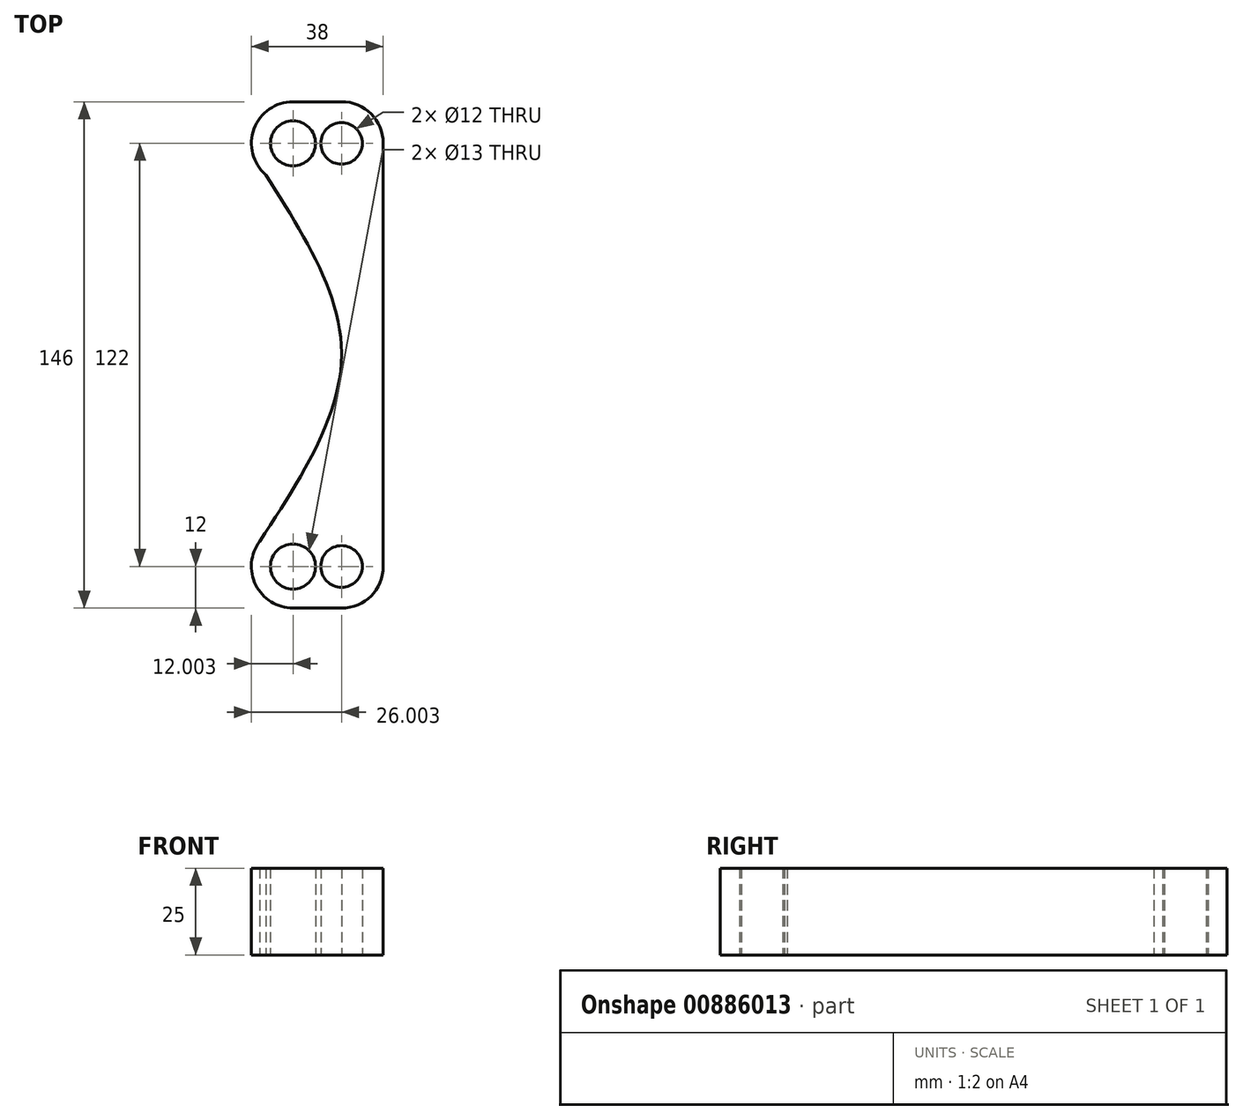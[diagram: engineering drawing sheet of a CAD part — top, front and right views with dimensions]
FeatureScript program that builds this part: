
annotation { "Feature Type Name" : "Feature", "Feature Type Description" : "" }
export const myFeature = defineFeature(function(context is Context, id is Id, definition is map)
    precondition{}
    {
        {
            var Q0;
            Q0=qCreatedBy(makeId("Top.planeOp"),FACE);
            var sketch = newSketch(context, id + "F0", { "sketchPlane" : qUnion([Q0])});
            skCircle(sketch, "E0", {"center": v(0, 0) * mm, "radius": 151 * mm, "construction": true});
            skCircle(sketch, "E1", {"center": v(0, 0) * mm, "radius": 70 * mm, "construction": true});
            skCircle(sketch, "E2", {"center": v(-34.34, 61) * mm, "radius": 6 * mm});
            skCircle(sketch, "E3", {"center": v(-34.34, -61) * mm, "radius": 6 * mm});
            skLineSegment(sketch, "E4", {"start": v(-34.34, -61) * mm, "end": v(-34.34, 61) * mm});
            skLineSegment(sketch, "E5", {"start": v(-151, 0) * mm, "end": v(-104, 0) * mm});
            skLineSegment(sketch, "E6", {"start": v(-70, 0) * mm, "end": v(-104, 0) * mm});
            skCircle(sketch, "E7", {"center": v(-48.34, 61) * mm, "radius": 6.5 * mm});
            skCircle(sketch, "E8", {"center": v(-48.34, -61) * mm, "radius": 6.5 * mm});
            skLineSegment(sketch, "E9", {"start": v(-34.34, -61) * mm, "end": v(-48.34, -61) * mm});
            skLineSegment(sketch, "E10", {"start": v(-34.34, 61) * mm, "end": v(-48.34, 61) * mm});
            skCircle(sketch, "E11", {"center": v(-34.34, 61) * mm, "radius": 12 * mm});
            skCircle(sketch, "E12", {"center": v(-48.34, 61) * mm, "radius": 12 * mm});
            skCircle(sketch, "E13", {"center": v(-48.34, -61) * mm, "radius": 12 * mm});
            skCircle(sketch, "E14", {"center": v(-34.34, -61) * mm, "radius": 12 * mm});
            skLineSegment(sketch, "E15", {"start": v(-22.34, -61) * mm, "end": v(-22.34, 61) * mm});
            skFitSpline(sketch, "E16", {"points": [v(-56.2, 51.93) * mm, v(-34.34, 0) * mm, v(-57.89, -53.74) * mm], "startDerivative": vector(66.64, -104.54) * mm, "endDerivative": vector(-69.54, -106.78) * mm});
            skLineSegment(sketch, "E17", {"start": v(-48.34, 73) * mm, "end": v(-34.34, 73) * mm});
            skLineSegment(sketch, "E18", {"start": v(-48.34, -73) * mm, "end": v(-34.34, -73) * mm});
            skSolve(sketch);
        }
        {
            var Q0;
            Q0 = qSketchRegion(id + "F0", true);
            var Q1;
            {var subQ5=sQuery(id+"F0.wireOp",EDGE,"E10");var subQ6=sQuery(id+"F0.wireOp",EDGE,"E2");var subQ7=makeQuery(id+"F0.imprint","INTERSECT",VERTEX,{"derivedFrom":[subQ6,subQ5]});Q1=makeQuery(id+"F0.imprint","IMPRINT",FACE,{"disambiguationData":[TD([[makeQuery(id+"F0.imprint","IMPRINT",EDGE,{"disambiguationData":[TD([[subQ7,-1.0]])],"derivedFrom":subQ6}),-1.0]])]});}
            var Q2;
            {var subQ5=sQuery(id+"F0.wireOp",EDGE,"E10");var subQ6=sQuery(id+"F0.wireOp",EDGE,"E2");var subQ7=makeQuery(id+"F0.imprint","INTERSECT",VERTEX,{"derivedFrom":[subQ6,subQ5]});Q2=makeQuery(id+"F0.imprint","IMPRINT",FACE,{"disambiguationData":[TD([[makeQuery(id+"F0.imprint","IMPRINT",EDGE,{"disambiguationData":[TD([[subQ7,1.0]])],"derivedFrom":subQ6}),-1.0]])]});}
            var Q3;
            {var subQ0=sQuery(id+"F0.wireOp",EDGE,"E12");var subQ1=sQuery(id+"F0.wireOp",EDGE,"E2");var subQ2=makeQuery(id+"F0.imprint","INTERSECT",VERTEX,{"disambiguationData":[OD(1.0)],"derivedFrom":[subQ1,subQ0]});Q3=makeQuery(id+"F0.imprint","IMPRINT",FACE,{"disambiguationData":[TD([[makeQuery(id+"F0.imprint","IMPRINT",EDGE,{"disambiguationData":[TD([[subQ2,-1.0]])],"derivedFrom":subQ1}),-1.0]])]});}
            var Q4;
            {var subQ0=sQuery(id+"F0.wireOp",EDGE,"E13");var subQ1=sQuery(id+"F0.wireOp",EDGE,"E3");var subQ2=makeQuery(id+"F0.imprint","INTERSECT",VERTEX,{"disambiguationData":[OD(0.0)],"derivedFrom":[subQ1,subQ0]});Q4=makeQuery(id+"F0.imprint","IMPRINT",FACE,{"disambiguationData":[TD([[makeQuery(id+"F0.imprint","IMPRINT",EDGE,{"disambiguationData":[TD([[subQ2,1.0]])],"derivedFrom":subQ1}),-1.0]])]});}
            var Q5;
            {var subQ1=sQuery(id+"F0.wireOp",EDGE,"E3");var subQ5=sQuery(id+"F0.wireOp",EDGE,"E13");var subQ6=makeQuery(id+"F0.imprint","INTERSECT",VERTEX,{"disambiguationData":[OD(0.0)],"derivedFrom":[subQ1,subQ5]});Q5=makeQuery(id+"F0.imprint","IMPRINT",FACE,{"disambiguationData":[TD([[makeQuery(id+"F0.imprint","IMPRINT",EDGE,{"disambiguationData":[TD([[subQ6,-1.0]])],"derivedFrom":subQ1}),-1.0]])]});}
            var Q6;
            {var subQ1=sQuery(id+"F0.wireOp",EDGE,"E3");var subQ5=sQuery(id+"F0.wireOp",EDGE,"E9");var subQ6=makeQuery(id+"F0.imprint","INTERSECT",VERTEX,{"derivedFrom":[subQ1,subQ5]});Q6=makeQuery(id+"F0.imprint","IMPRINT",FACE,{"disambiguationData":[TD([[makeQuery(id+"F0.imprint","IMPRINT",EDGE,{"disambiguationData":[TD([[subQ6,-1.0]])],"derivedFrom":subQ1}),-1.0]])]});}
            extrude(context, id + "F1", {"entities" : qUnion([Q0, Q1, Q2, Q3, Q4, Q5, Q6]), "depth" : 25 * mm, "offsetDistance" : 25 * mm});
        }
    });
